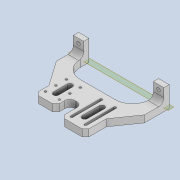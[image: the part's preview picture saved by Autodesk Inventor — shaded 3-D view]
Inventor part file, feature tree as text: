
AUTODESK INVENTOR PART (.ipt)
format: ipt  version: 2020 (Build 240168000, 168)  size: 353,280 bytes
history: native  units: mm
features: reference x10, projected_geometry x9, extrude x8, sketch x8, other x6, thicken_offset x3, fillet x3, plane x1, chamfer x1
ambient origin geometry x8: Origin, YZ Plane, XZ Plane, XY Plane, X Axis, Y Axis, Z Axis, Center Point
bodies: Solid1 (feature_tree)
feature tree (49):
  extrude  "Extrusion1"  Depth=20.0mm
  plane  "Work Plane1"
  extrude  "Extrusion2"  Depth=20.0mm
  extrude  "Extrusion3"  Depth=3.0mm
  extrude  "Extrusion4"  Depth=12.0mm
  thicken_offset  "Thicken1"
  extrude  "Extrusion5"  Depth=4.0mm TaperAngle=0.0deg
  extrude  "Extrusion6"  Depth=24.0mm
  thicken_offset  "Thicken2"
  thicken_offset  "Thicken3"
  fillet  "Fillet1"  Radius=12.0mm
  extrude  "Extrusion7"  Depth=4.0mm TaperAngle=0.0deg
  fillet  "Fillet2"  Radius=12.0mm
  chamfer  "Chamfer1"  Distance=4.0mm
  fillet  "Fillet3"  Radius=17.0mm
  extrude  "Extrusion8"  Depth=12.0mm
  sketch  "Sketch1"  dims[d0=6.0mm d1=20.0mm]
  reference  "Reference1"
  reference  "Reference2"
  sketch  "Sketch2"  dims[d2=6.0mm d3=20.0mm]
  projected_geometry  "Projected Loop1"
  projected_geometry  "Projected Loop2"
  sketch  "Sketch3"  dims[d4=3.0mm d5=0.0mm d6=40.0mm]
  projected_geometry  "Projected Loop3"
  sketch  "Sketch4"  dims[d7=12.0mm d8=52.0mm]
  projected_geometry  "Projected Loop4"
  projected_geometry  "Projected Loop5"
  projected_geometry  "Projected Loop6"
  sketch  "Sketch5"  dims[d9=24.0mm d10=4.0mm d11=0.0mm]
  reference  "Reference3"
  reference  "Reference4"
  reference  "Reference5"
  reference  "Reference6"
  reference  "Reference7"
  reference  "Reference8"
  sketch  "Sketch6"  dims[d12=12.0mm d13=24.0mm d14=12.0mm]
  projected_geometry  "Projected Loop7"
  reference  "Reference9"
  reference  "Reference10"
  sketch  "Sketch7"  dims[d15=24.0mm d16=4.0mm d17=0.0mm d18=12.0mm d19=0.0mm]
  projected_geometry  "Projected Loop8"
  sketch  "Sketch8"  dims[d20=4.0mm d21=4.0mm d22=17.0mm d23=1.3mm d24=17.0mm d25=1.3mm d26=12.0mm d27=0.0mm d28=12.0mm d29=0.0mm d30=1.0mm d31=1.0mm d32=1.0mm d33=1.0mm d34=10.0mm d35=9.599311mm d36=9.599311mm d37=12.0mm d38=0.0mm d39=3.0mm d40=2.0mm d41=2.0mm d42=45.0deg d43=3.0mm d44=4.0mm d45=3.0mm d46=5.0mm d47=3.0mm d48=12.0mm d49=0.0mm]
  projected_geometry  "Projected Loop9"
  parser-record x1  (decoder bookkeeping rows leaked as tree rows — omitted from the tree; the rows remain in map.json)
  other  "tip_3_n_base.iam"
  other  "cpr_shell_1:1"
  other  "bl_tube_ass_2:2"
  other  "bl_tube_hn_1:1"
  other  "bl_tube_ass_2:1"
note: 1 file-system path scrubbed to <path> (originals preserved in map.json)
